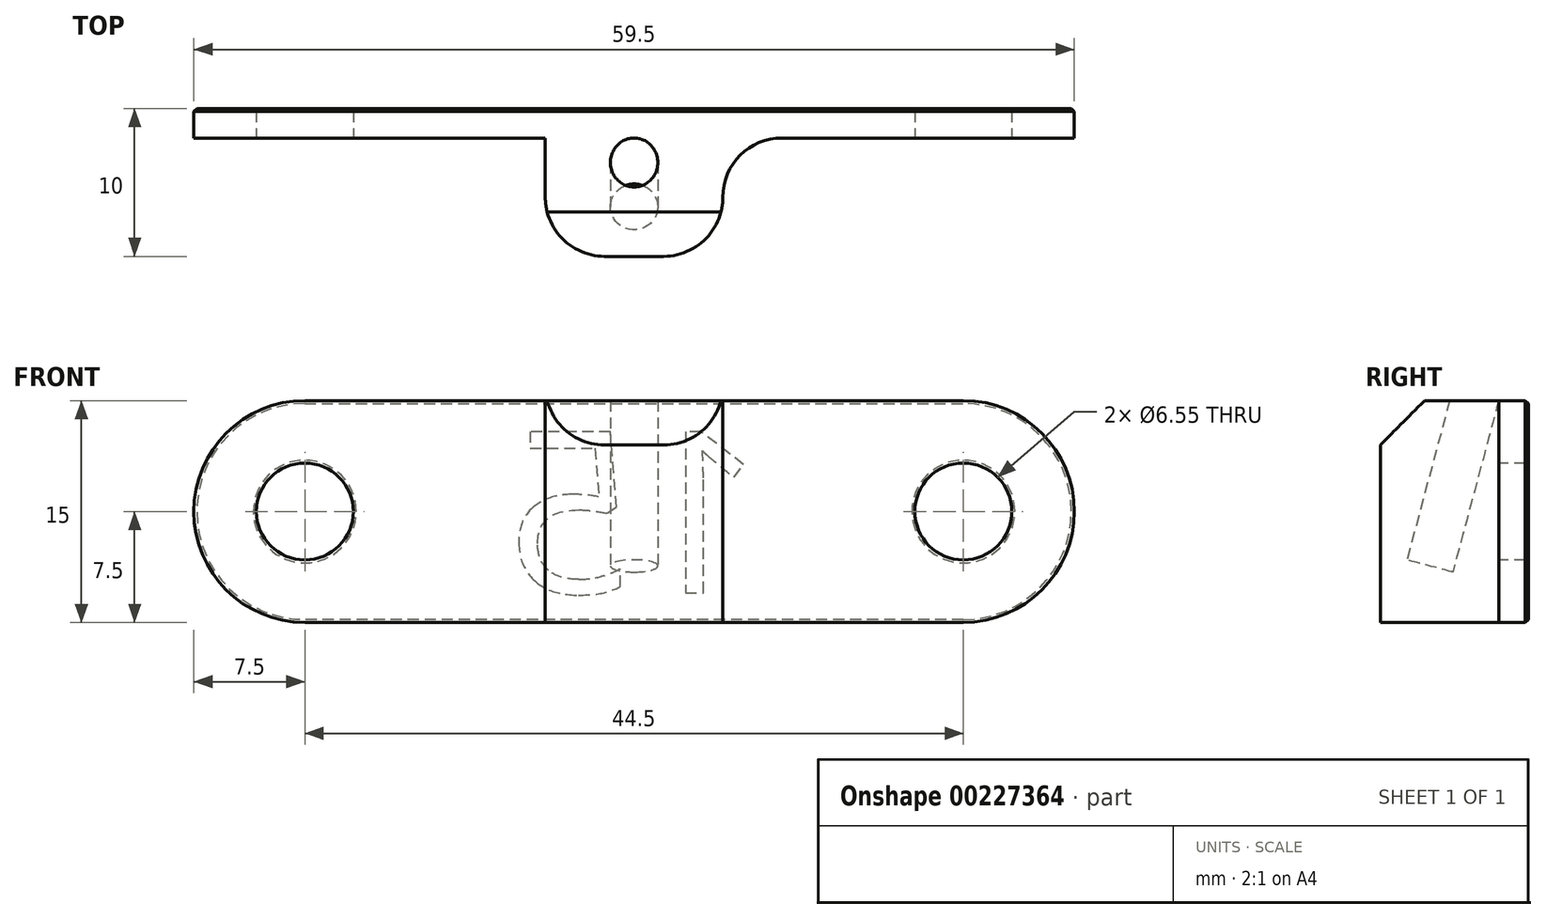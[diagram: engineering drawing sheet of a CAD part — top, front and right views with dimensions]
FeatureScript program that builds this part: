
annotation { "Feature Type Name" : "Feature", "Feature Type Description" : "" }
export const myFeature = defineFeature(function(context is Context, id is Id, definition is map)
    precondition{}
    {
        {
            var Q0;
            Q0=qCreatedBy(makeId("Front.planeOp"),FACE);
            var sketch = newSketch(context, id + "F0", { "sketchPlane" : qUnion([Q0])});
            skCircle(sketch, "E0", {"center": v(-22.25, 0) * mm, "radius": 3.28 * mm});
            skCircle(sketch, "E1", {"center": v(22.25, 0) * mm, "radius": 3.28 * mm});
            skLineSegment(sketch, "E2", {"start": v(-22.25, 0) * mm, "end": v(22.25, 0) * mm, "construction": true});
            skArc(sketch, "E3.0.startCap", {"start": v(-22.25, -7.5) * mm, "mid": v(-29.75, 0) * mm, "end": v(-22.25, 7.5) * mm});
            skArc(sketch, "E3.0.endCap", {"start": v(22.25, 7.5) * mm, "mid": v(29.75, 0) * mm, "end": v(22.25, -7.5) * mm});
            skLineSegment(sketch, "E3.0.left", {"start": v(-22.25, 7.5) * mm, "end": v(22.25, 7.5) * mm});
            skLineSegment(sketch, "E3.0.right", {"start": v(-22.25, -7.5) * mm, "end": v(22.25, -7.5) * mm});
            skSolve(sketch);
        }
        {
            var Q0;
            Q0=qSketchRegion(id+"F0",true);
            extrude(context, id + "F1", {"entities" : qUnion([Q0]), "oppositeDirection" : true, "depth" : 2 * mm, "offsetDistance" : 25 * mm});
        }
        {
            var Q0;
            Q0=qCreatedBy(makeId("Right.planeOp"),FACE);
            var sketch = newSketch(context, id + "F2", { "sketchPlane" : qUnion([Q0])});
            skLineSegment(sketch, "E4", {"start": v(-3.1, -4.1) * mm, "end": v(8.88, 40.64) * mm});
            skLineSegment(sketch, "E5", {"start": v(8.88, 40.64) * mm, "end": v(5.79, 41.47) * mm});
            skLineSegment(sketch, "E6", {"start": v(5.79, 41.47) * mm, "end": v(-6.2, -3.26) * mm});
            skLineSegment(sketch, "E7", {"start": v(-6.2, -3.26) * mm, "end": v(-3.1, -4.1) * mm});
            skLineSegment(sketch, "E8.0.0", {"start": v(0, -7.5) * mm, "end": v(0, 7.5) * mm, "construction": true});
            skLineSegment(sketch, "E8.0.2", {"start": v(0, -7.5) * mm, "end": v(0, 7.5) * mm, "construction": true});
            skLineSegment(sketch, "E9", {"start": v(7.34, 41.06) * mm, "end": v(-4.65, -3.68) * mm});
            skSolve(sketch);
        }
        {
            var Q0;
            Q0=qCreatedBy(makeId("Right.planeOp"),FACE);
            var sketch = newSketch(context, id + "F3", { "sketchPlane" : qUnion([Q0])});
            skLineSegment(sketch, "E10.0.0", {"start": v(0, -7.5) * mm, "end": v(0, 7.5) * mm, "construction": true});
            skLineSegment(sketch, "E10.0.2", {"start": v(0, -7.5) * mm, "end": v(0, 7.5) * mm, "construction": true});
            skLineSegment(sketch, "E11.bottom", {"start": v(0, 7.5) * mm, "end": v(-8, 7.5) * mm});
            skLineSegment(sketch, "E11.top", {"start": v(0, -7.5) * mm, "end": v(-8, -7.5) * mm});
            skLineSegment(sketch, "E11.left", {"start": v(0, 7.5) * mm, "end": v(0, -7.5) * mm});
            skLineSegment(sketch, "E11.right", {"start": v(-8, 7.5) * mm, "end": v(-8, -7.5) * mm});
            skSolve(sketch);
        }
        {
            var Q0;
            Q0=qSketchRegion(id+"F3",true);
            extrude(context, id + "F4", {"entities" : qUnion([Q0]), "operationType" : NewBodyOperationType.ADD, "endBound" : BoundingType.SYMMETRIC, "depth" : 12 * mm, "offsetDistance" : 25 * mm});
        }
        {
            var Q0;
            Q0=makeQuery(id+"F4.opExtrude","SWEPT_EDGE",EDGE,{"disambiguationData":[OSD([sQuery(id+"F3.wireOp",EDGE,"E11.bottom"),sQuery(id+"F3.wireOp",EDGE,"E11.right")])]});
            chamfer(context, id + "F5", {"entities" : qUnion([Q0]), "width" : 3 * mm});
        }
        {
            var Q0;
            Q0=makeQuery(id+"F4.opExtrude","SWEPT_EDGE",EDGE,{"disambiguationData":[OSD([sQuery(id+"F3.wireOp",EDGE,"E11.top"),sQuery(id+"F3.wireOp",EDGE,"E11.left")])]});
            var Q1;
            Q1=makeQuery(id+"F4.opExtrude","CAP_EDGE",EDGE,{"disambiguationData":[OSD([sQuery(id+"F3.wireOp",EDGE,"E11.left")])],"isStart":false});
            var Q2;
            Q2=makeQuery(id+"F4.opExtrude","CAP_EDGE",EDGE,{"disambiguationData":[OSD([sQuery(id+"F3.wireOp",EDGE,"E11.left")])],"isStart":true});
            var Q3;
            Q3=makeQuery(id+"F4.opExtrude","CAP_EDGE",EDGE,{"disambiguationData":[OSD([sQuery(id+"F3.wireOp",EDGE,"E11.right")])],"isStart":false});
            var Q4;
            Q4=makeQuery(id+"F4.opExtrude","CAP_EDGE",EDGE,{"disambiguationData":[OSD([sQuery(id+"F3.wireOp",EDGE,"E11.right")])],"isStart":true});
            fillet(context, id + "F6", {"entities" : qUnion([Q0, Q1, Q2, Q3, Q4]), "radius" : 4 * mm, "allowEdgeOverflow" : false});
        }
        {
            var Q0;
            {var subQ0=sQuery(id+"F2.wireOp",EDGE,"E6");Q0=makeQuery(id+"F2.imprint","IMPRINT",FACE,{"disambiguationData":[TD([[makeQuery(id+"F2.imprint","IMPRINT",EDGE,{"derivedFrom":subQ0}),1.0]])]});}
            var Q1;
            Q1=sQuery(id+"F2.wireOp",EDGE,"E9");
            revolve(context, id + "F7", {"operationType" : NewBodyOperationType.REMOVE, "entities" : qUnion([Q0]), "axis" : qUnion([Q1]), "revolveType" : RevolveType.FULL, "oppositeDirection" : true});
        }
        {
            var Q0;
            Q0=makeQuery(id+"F1.opExtrude","CAP_FACE",FACE,{"disambiguationData":[OSD([sQuery(id+"F0.wireOp",EDGE,"E0"),sQuery(id+"F0.wireOp",EDGE,"E1"),sQuery(id+"F0.wireOp",EDGE,"E3.0.startCap"),sQuery(id+"F0.wireOp",EDGE,"E3.0.endCap"),sQuery(id+"F0.wireOp",EDGE,"E3.0.left"),sQuery(id+"F0.wireOp",EDGE,"E3.0.right")])],"isStart":false});
            chamfer(context, id + "F8", {"entities" : qUnion([Q0]), "width" : 0.2 * mm});
        }
        {
            var Q0;
            Q0=makeQuery(id+"F1.opExtrude","CAP_FACE",FACE,{"disambiguationData":[OSD([sQuery(id+"F0.wireOp",EDGE,"E0"),sQuery(id+"F0.wireOp",EDGE,"E1"),sQuery(id+"F0.wireOp",EDGE,"E3.0.startCap"),sQuery(id+"F0.wireOp",EDGE,"E3.0.endCap"),sQuery(id+"F0.wireOp",EDGE,"E3.0.left"),sQuery(id+"F0.wireOp",EDGE,"E3.0.right")])],"isStart":false});
            var sketch = newSketch(context, id + "F9", { "sketchPlane" : qUnion([Q0])});
            skText(sketch, "E12", { "text": "15", "fontName": "OpenSans-Regular.ttf"});
            const initialGuessF9  = {"E12": [-0.0088, -0.0055, 1, 0, 0.011]};
            skSetInitialGuess(sketch, initialGuessF9);
            skSolve(sketch);
        }
        {
            var Q0;
            Q0 = qSketchRegion(id + "F9", true);
            extrude(context, id + "F10", {"entities" : qUnion([Q0]), "operationType" : NewBodyOperationType.REMOVE, "oppositeDirection" : true, "depth" : 0.2 * mm, "offsetDistance" : 25 * mm});
        }
    });
